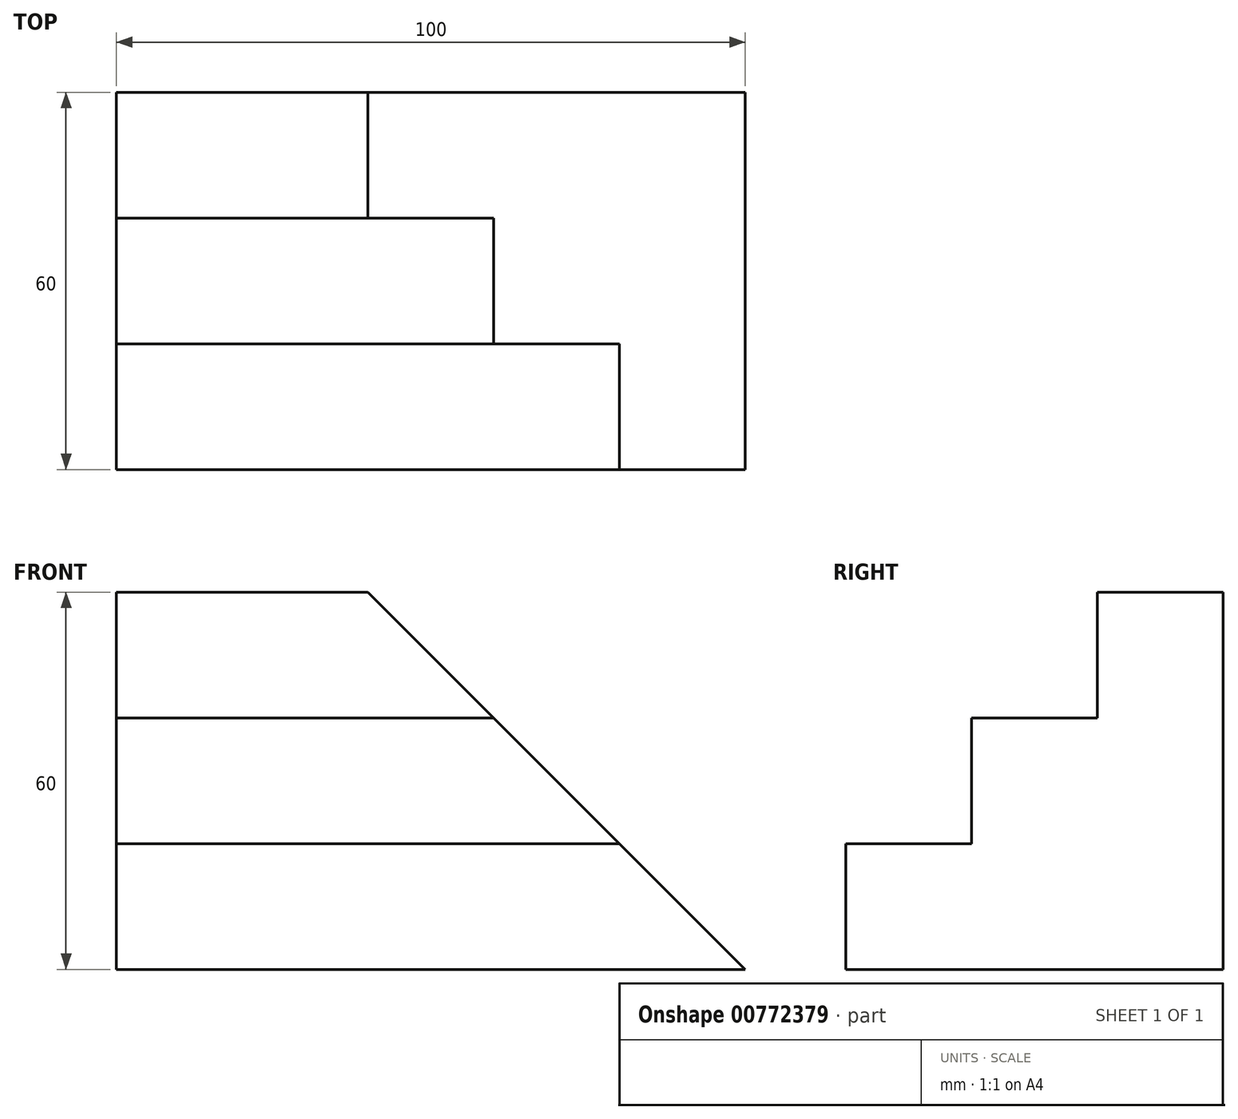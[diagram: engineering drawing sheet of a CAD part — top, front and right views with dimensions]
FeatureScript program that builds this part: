
annotation { "Feature Type Name" : "Feature", "Feature Type Description" : "" }
export const myFeature = defineFeature(function(context is Context, id is Id, definition is map)
    precondition{}
    {
        {
            var Q0;
            Q0=qCreatedBy(makeId("Right.planeOp"),FACE);
            var sketch = newSketch(context, id + "F0", { "sketchPlane" : qUnion([Q0])});
            skLineSegment(sketch, "E0", {"start": v(0, 0) * mm, "end": v(0, 60) * mm});
            skLineSegment(sketch, "E1", {"start": v(0, 60) * mm, "end": v(-20, 60) * mm});
            skLineSegment(sketch, "E2", {"start": v(-20, 60) * mm, "end": v(-20, 40) * mm});
            skLineSegment(sketch, "E3", {"start": v(-20, 40) * mm, "end": v(-40, 40) * mm});
            skLineSegment(sketch, "E4", {"start": v(-40, 40) * mm, "end": v(-40, 20) * mm});
            skLineSegment(sketch, "E5", {"start": v(-40, 20) * mm, "end": v(-60, 20) * mm});
            skLineSegment(sketch, "E6", {"start": v(-60, 20) * mm, "end": v(-60, 0) * mm});
            skLineSegment(sketch, "E7", {"start": v(-60, 0) * mm, "end": v(0, 0) * mm});
            skSolve(sketch);
        }
        {
            var Q0;
            Q0 = qSketchRegion(id + "F0", true);
            extrude(context, id + "F1", {"entities" : qUnion([Q0]), "depth" : 100 * mm, "offsetDistance" : 25 * mm});
        }
        {
            var Q0;
            Q0=makeQuery(id+"F1.opExtrude","CAP_EDGE",EDGE,{"disambiguationData":[OSD([sQuery(id+"F0.wireOp",EDGE,"E1")])],"isStart":false});
            chamfer(context, id + "F2", {"entities" : qUnion([Q0]), "width" : 60 * mm, "tangentPropagation" : true});
        }
    });
